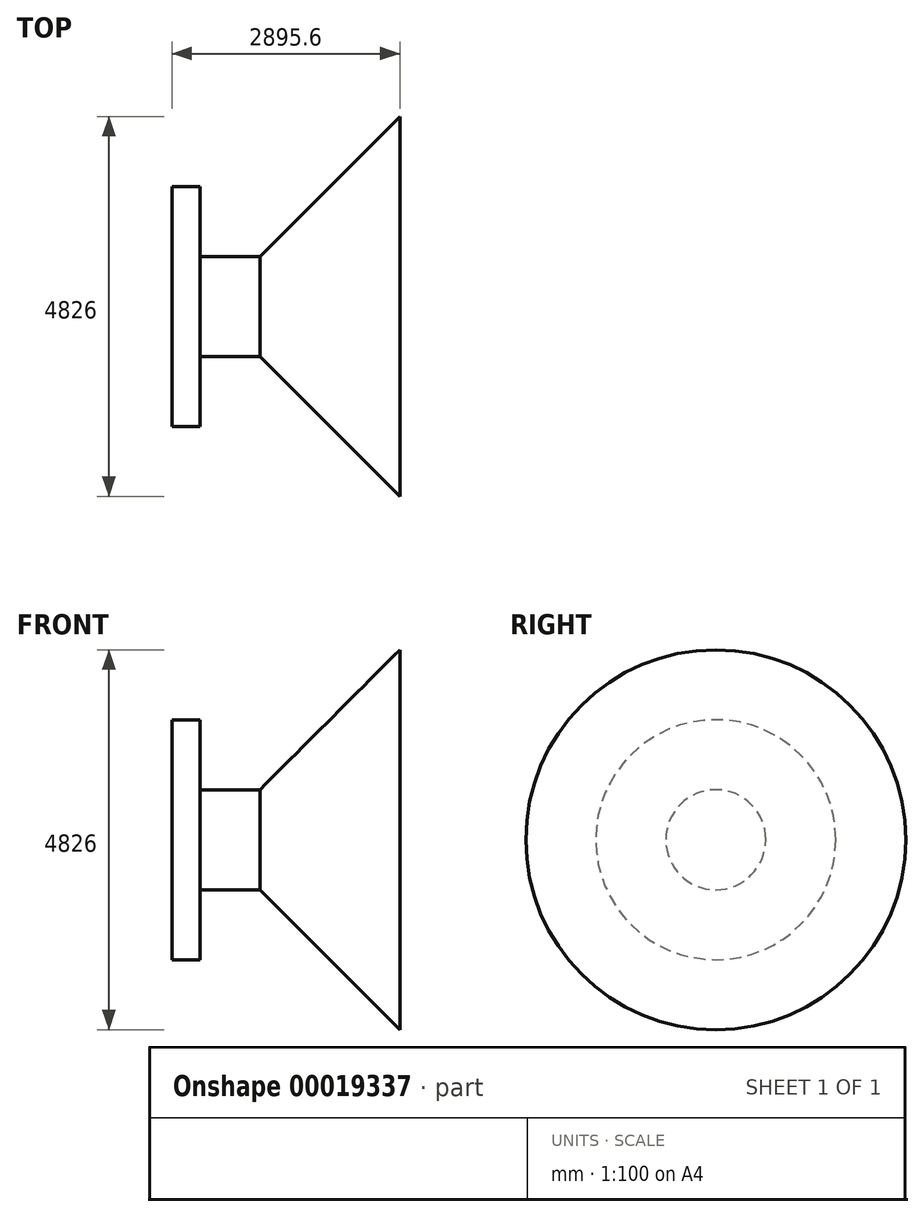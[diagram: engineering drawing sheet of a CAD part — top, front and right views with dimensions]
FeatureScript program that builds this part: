
annotation { "Feature Type Name" : "Feature", "Feature Type Description" : "" }
export const myFeature = defineFeature(function(context is Context, id is Id, definition is map)
    precondition{}
    {
        {
            var Q0;
            Q0=qCreatedBy(makeId("Top.planeOp"),FACE);
            var sketch = newSketch(context, id + "F0", { "sketchPlane" : qUnion([Q0])});
            skLineSegment(sketch, "E0", {"start": v(0, 0) * mm, "end": v(0, 1524) * mm});
            skLineSegment(sketch, "E1", {"start": v(0, 1524) * mm, "end": v(355.6, 1524) * mm});
            skLineSegment(sketch, "E2", {"start": v(355.6, 1524) * mm, "end": v(355.6, 635) * mm});
            skLineSegment(sketch, "E3", {"start": v(355.6, 635) * mm, "end": v(1117.6, 635) * mm});
            skLineSegment(sketch, "E4", {"start": v(1117.6, 635) * mm, "end": v(2895.6, 2413) * mm});
            skLineSegment(sketch, "E5", {"start": v(2895.6, 2413) * mm, "end": v(2895.6, 0) * mm});
            skLineSegment(sketch, "E6", {"start": v(2895.6, 0) * mm, "end": v(0, 0) * mm, "construction": true});
            skLineSegment(sketch, "E7", {"start": v(1117.6, 635) * mm, "end": v(1117.6, 0) * mm, "construction": true});
            skLineSegment(sketch, "E8", {"start": v(0, 0) * mm, "end": v(2895.6, 0) * mm});
            skSolve(sketch);
        }
        {
            var Q0;
            Q0 = qSketchRegion(id + "F0", true);
            var Q1;
            Q1=sQuery(id+"F0.wireOp",EDGE,"E8");
            revolve(context, id + "F1", {"entities" : qUnion([Q0]), "axis" : qUnion([Q1]), "revolveType" : RevolveType.FULL});
        }
    });
